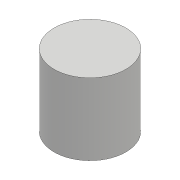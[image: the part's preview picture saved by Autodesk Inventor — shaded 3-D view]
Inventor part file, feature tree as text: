
AUTODESK INVENTOR PART (.ipt)
format: ipt  version: 2017 (Build 210142000, 142)  size: 70,656 bytes
history: native  units: mm
features: extrude x1, sketch x1
ambient origin geometry x8: Origin, YZ Plane, XZ Plane, XY Plane, X Axis, Y Axis, Z Axis, Center Point
bodies: Solid1 (feature_tree)
feature tree (2):
  extrude  "Extrusion1"  Depth=10.0mm TaperAngle=0.0deg
  sketch  "Sketch1"  dims[d0=10.0mm d1=10.0mm d2=0.0mm]
